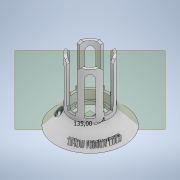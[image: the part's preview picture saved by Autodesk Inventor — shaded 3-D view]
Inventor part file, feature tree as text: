
AUTODESK INVENTOR PART (.ipt)
format: ipt  version: 2022.4 (Build 264492010, 492A)  size: 1,082,368 bytes
history: native  units: in
note: dims shown in document units (in); Inventor stores cm internally (conversion verified against a paired STEP export)
features: sketch x11, extrude x8, plane x3, pattern_circular x3, revolve x2, emboss x1
ambient origin geometry x8: Origin, YZ Plane, XZ Plane, XY Plane, X Axis, Y Axis, Z Axis, Center Point
bodies: Solid1 (feature_tree)
feature tree (28):
  extrude  "Extrusion1"  Depth=0.2559in
  plane  "Work Plane1"
  extrude  "Extrusion3"  Depth=2.3622in
  extrude  "Extrusion4"  TaperAngle=0.0deg  [1 undecoded]
  extrude  "Extrusion5"  Depth=2.2835in
  extrude  "Extrusion6"  Depth=0.1969in
  pattern_circular  "Circular Pattern2"  Count=10  [1 undecoded]
  extrude  "Extrusion7"  Depth=0.2559in
  revolve  "Revolution3"  Angle=360.0deg
  extrude  "Extrusion8"  TaperAngle=0.0deg  [1 undecoded]
  pattern_circular  "Circular Pattern4"  Count=7  [1 undecoded]
  emboss  "Emboss4"
  extrude  "Extrusion9"  Depth=0.1575in TaperAngle=0.0deg
  plane  "Work Plane5"
  sketch  "Sketch23"  dims[d54=3.248in d55=0.1575in d56=0.0in]
  plane  "Work Plane4"
  revolve  "Revolution5"  [1 undecoded]
  pattern_circular  "Circular Pattern5"  [2 undecoded]
  sketch  "Sketch1"  dims[d2=0.1969in d3=0.0in d10=0.2559in]
  sketch  "Sketch5"  dims[d11=2.5984in d12=2.3622in]
  sketch  "Sketch6"  dims[d13=0.1969in d14=0.0in d15=0.0in]
  sketch  "Sketch7"  dims[d16=2.5197in d17=2.2835in]
  sketch  "Sketch13"  dims[d18=0.0787in d19=0.0in d22=0.1969in d23=3.937in d24=0.0in]
  sketch  "Sketch14"  dims[d25=0.2559in d26=0.0in d40=3.7008in]
  sketch  "Sketch17"  dims[d43=0.0in d44=0.0in d45=3.1496in d46=360.0deg]
  sketch  "Sketch20"  dims[d49=0.5906in d50=0.0in]
  sketch  "Sketch21"  dims[d51=0.6299in d52=2.7559in]
  sketch  "Sketch24"  dims[d60=0.1969in d61=0.1969in d62=0.1969in d63=360.0deg d81=0.5906in d82=0.0in d83=0.7874in d85=0.0in d86=0.0in d87=1.5748in d88=360.0deg d98=0.0787in d102=0.315in d103=0.1969in d104=0.1969in d106=0.1969in d107=0.1969in d108=0.0787in d109=0.0in d110=0.315in d111=2.6772in d112=2.6772in d113=0.0787in d121=0.4331in d122=1.5748in d124=360.0deg d126=0.1378in d127=0.0in d130=135.0deg d137=90.0deg d138=0.1772in d139=1.5748in d140=360.0deg d68=0.0344in d69=0.0344in d72=0.0344in d73=0.0344in d131=0.0344in d132=0.0197in d133=0.0344in]
note: 7 required parameter values undecoded (feature->parameter linkage not recoverable at this tier; creation-order binding heuristic only, values carry confidence <= 0.55)